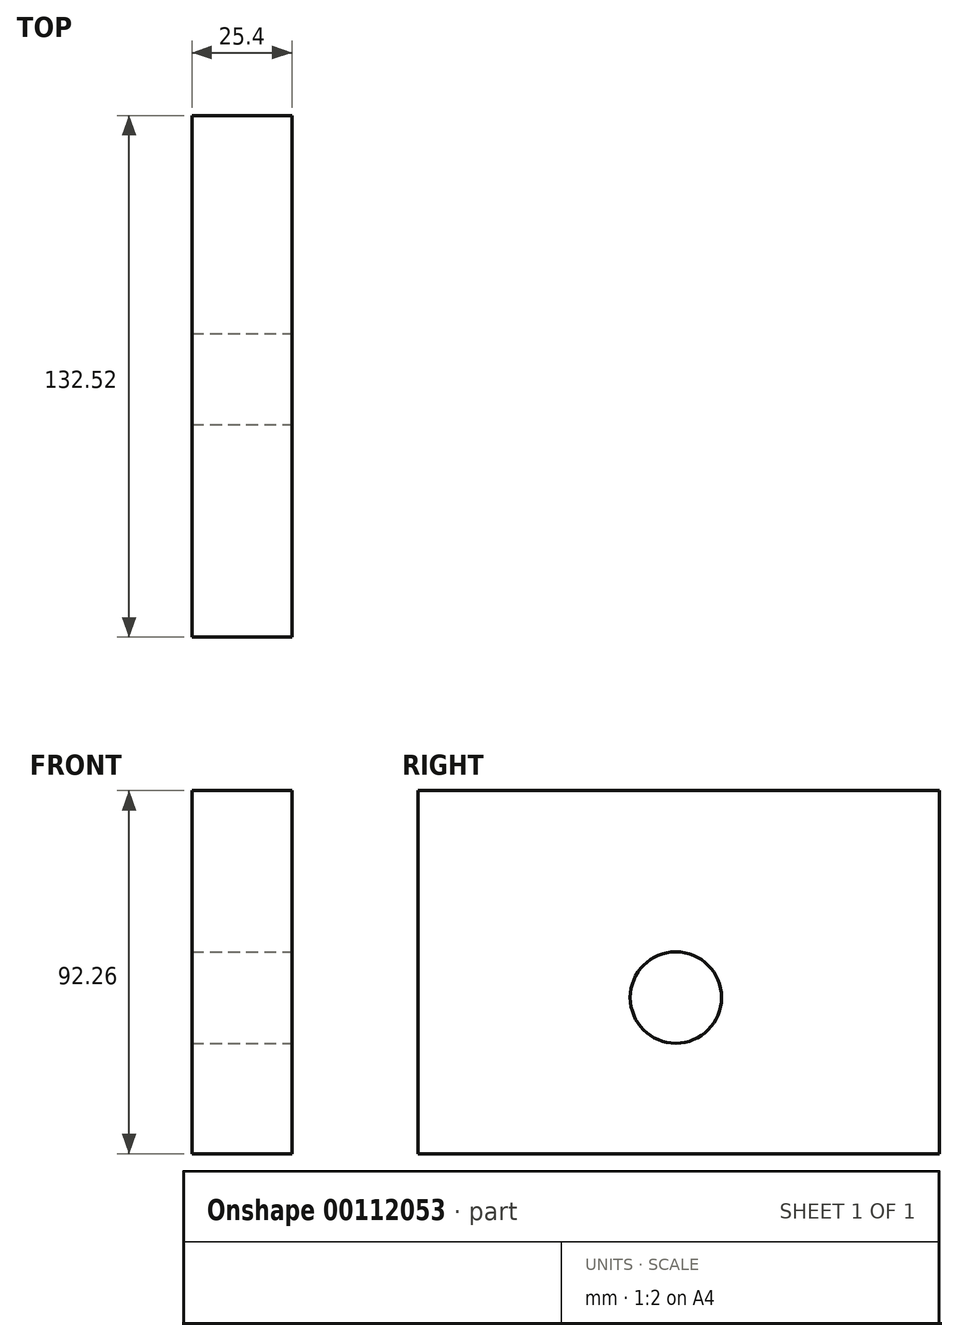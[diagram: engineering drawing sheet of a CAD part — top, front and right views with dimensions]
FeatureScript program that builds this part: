
annotation { "Feature Type Name" : "Feature", "Feature Type Description" : "" }
export const myFeature = defineFeature(function(context is Context, id is Id, definition is map)
    precondition{}
    {
        {
            var Q0;
            Q0=qCreatedBy(makeId("Right.planeOp"),FACE);
            var sketch = newSketch(context, id + "F0", { "sketchPlane" : qUnion([Q0])});
            skLineSegment(sketch, "E0.bottom", {"start": v(88.35, -39.67) * mm, "end": v(-44.17, -39.67) * mm});
            skLineSegment(sketch, "E0.top", {"start": v(88.35, 52.6) * mm, "end": v(-44.17, 52.6) * mm});
            skLineSegment(sketch, "E0.left", {"start": v(88.35, -39.67) * mm, "end": v(88.35, 52.6) * mm});
            skLineSegment(sketch, "E0.right", {"start": v(-44.17, -39.67) * mm, "end": v(-44.17, 52.6) * mm});
            skSolve(sketch);
        }
        {
            var Q0;
            Q0=makeQuery(id+"F0.imprint","IMPRINT",FACE,{"disambiguationData":[TD([[makeQuery(id+"F0.imprint","IMPRINT",EDGE,{"derivedFrom":sQuery(id+"F0.wireOp",EDGE,"E0.bottom")}),-1.0]])]});
            extrude(context, id + "F1", {"entities" : qUnion([Q0]), "depth" : 25.4 * mm});
        }
        {
            var Q0;
            Q0=makeQuery(id+"F1.opExtrude","CAP_FACE",FACE,{"disambiguationData":[OSD([sQuery(id+"F0.wireOp",EDGE,"E0.bottom"),sQuery(id+"F0.wireOp",EDGE,"E0.top"),sQuery(id+"F0.wireOp",EDGE,"E0.left"),sQuery(id+"F0.wireOp",EDGE,"E0.right")])],"isStart":false});
            var sketch = newSketch(context, id + "F2", { "sketchPlane" : qUnion([Q0])});
            skCircle(sketch, "E1", {"center": v(21.38, 0) * mm, "radius": 11.6 * mm});
            skSolve(sketch);
        }
        {
            var Q0;
            Q0=makeQuery(id+"F2.imprint","IMPRINT",FACE,{"disambiguationData":[TD([[makeQuery(id+"F2.imprint","IMPRINT",EDGE,{"derivedFrom":sQuery(id+"F2.wireOp",EDGE,"E1")}),1.0]])]});
            extrude(context, id + "F3", {"entities" : qUnion([Q0]), "operationType" : NewBodyOperationType.REMOVE, "oppositeDirection" : true, "depth" : 25.4 * mm});
        }
    });
